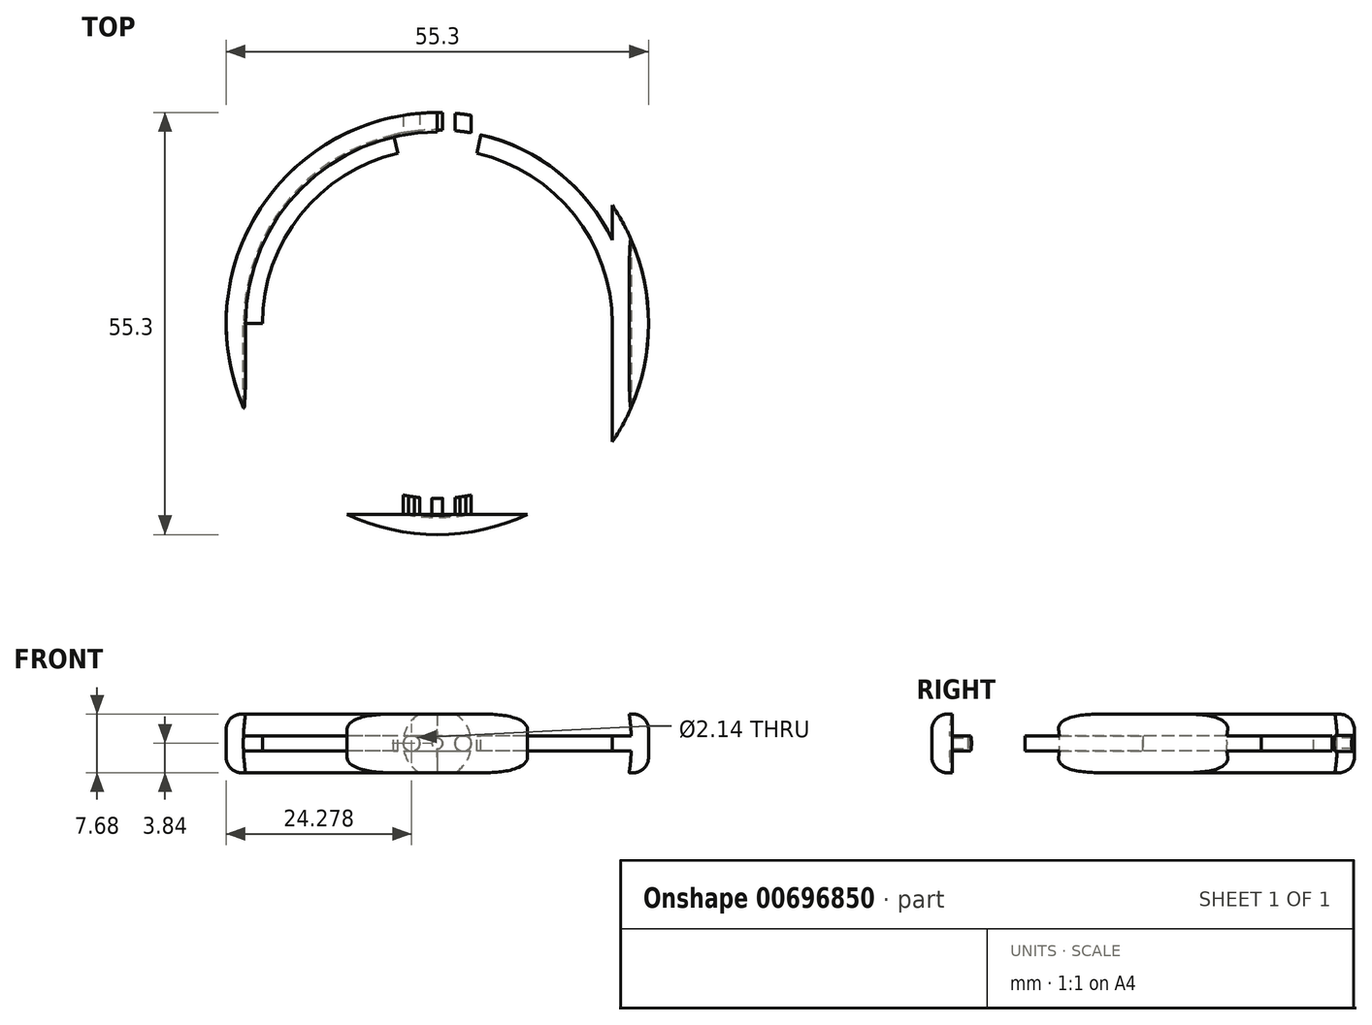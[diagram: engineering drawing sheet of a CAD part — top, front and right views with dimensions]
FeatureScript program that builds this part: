
annotation { "Feature Type Name" : "Feature", "Feature Type Description" : "" }
export const myFeature = defineFeature(function(context is Context, id is Id, definition is map)
    precondition{}
    {
        {
            var Q0;
            Q0=qCreatedBy(makeId("Top.planeOp"),FACE);
            var sketch = newSketch(context, id + "F0", { "sketchPlane" : qUnion([Q0])});
            skCircle(sketch, "E0", {"center": v(0, 0) * mm, "radius": 25.4 * mm});
            skLineSegment(sketch, "E1", {"start": v(-73.41, 0) * mm, "end": v(75.43, 0) * mm});
            skLineSegment(sketch, "E2", {"start": v(0, 25.4) * mm, "end": v(0, -25.4) * mm});
            skCircle(sketch, "E3", {"center": v(0, 0) * mm, "radius": 28.9 * mm});
            skLineSegment(sketch, "E4", {"start": v(-26.6, 11.29) * mm, "end": v(-22.75, 11.29) * mm});
            skLineSegment(sketch, "E5", {"start": v(-26.6, -11.29) * mm, "end": v(-22.75, -11.29) * mm});
            skLineSegment(sketch, "E6", {"start": v(22.75, -11.29) * mm, "end": v(26.6, -11.29) * mm});
            skLineSegment(sketch, "E7", {"start": v(22.75, 11.29) * mm, "end": v(26.6, 11.29) * mm});
            skCircle(sketch, "E8", {"center": v(0, 0) * mm, "radius": 22.72 * mm});
            skCircle(sketch, "E9", {"center": v(0, 0) * mm, "radius": 2.5 * mm});
            skLineSegment(sketch, "E10", {"start": v(0, -25.4) * mm, "end": v(0, -28.9) * mm, "construction": true});
            skSolve(sketch);
        }
        {
            var Q0;
            Q0=qCreatedBy(makeId("Front.planeOp"),FACE);
            var sketch = newSketch(context, id + "F1", { "sketchPlane" : qUnion([Q0])});
            skCircle(sketch, "E11", {"center": v(0, 0) * mm, "radius": 25.4 * mm});
            skLineSegment(sketch, "E12", {"start": v(-25.1, -3.84) * mm, "end": v(-27.65, -3.84) * mm});
            skLineSegment(sketch, "E13", {"start": v(-25.1, 3.84) * mm, "end": v(-27.65, 3.84) * mm});
            skLineSegment(sketch, "E14", {"start": v(-27.65, 3.84) * mm, "end": v(-27.65, -3.84) * mm});
            skLineSegment(sketch, "E15", {"start": v(0, 45.98) * mm, "end": v(0, -45.96) * mm});
            skLineSegment(sketch, "E16", {"start": v(25.38, -1) * mm, "end": v(22.9, -1) * mm});
            skLineSegment(sketch, "E17", {"start": v(22.9, -1) * mm, "end": v(22.9, 1) * mm});
            skLineSegment(sketch, "E18", {"start": v(22.9, 1) * mm, "end": v(25.38, 1) * mm});
            skCircle(sketch, "E19", {"center": v(-3.37, 0) * mm, "radius": 1.07 * mm});
            skCircle(sketch, "E20.MirrorC", {"center": v(3.37, 0) * mm, "radius": 1.07 * mm});
            skCircle(sketch, "E21", {"center": v(0, 0) * mm, "radius": 0.7 * mm});
            skSolve(sketch);
        }
        {
            var Q0;
            {var subQ0=sQuery(id+"F1.wireOp",EDGE,"E12");Q0=makeQuery(id+"F1.imprint","IMPRINT",FACE,{"disambiguationData":[TD([[makeQuery(id+"F1.imprint","IMPRINT",EDGE,{"derivedFrom":subQ0}),-1.0]])]});}
            var Q1;
            Q1=sQuery(id+"F1.wireOp",EDGE,"E15");
            revolve(context, id + "F2", {"entities" : qUnion([Q0]), "axis" : qUnion([Q1]), "revolveType" : RevolveType.FULL});
        }
        {
            var Q0;
            Q0=makeQuery(id+"F2.opRevolve","SWEPT_FACE",FACE,{"disambiguationData":[OSD([sQuery(id+"F1.wireOp",EDGE,"E13")])]});
            var sketch = newSketch(context, id + "F3", { "sketchPlane" : qUnion([Q0])});
            skLineSegment(sketch, "E22", {"start": v(-8.5, -23.63) * mm, "end": v(-8.5, -26.3) * mm});
            skLineSegment(sketch, "E23", {"start": v(8.5, -23.63) * mm, "end": v(8.5, -26.3) * mm});
            skLineSegment(sketch, "E24.MirrorCS", {"start": v(8.5, 23.63) * mm, "end": v(8.5, 26.3) * mm});
            skLineSegment(sketch, "E25.MirrorCS", {"start": v(-8.5, 23.63) * mm, "end": v(-8.5, 26.3) * mm});
            skSolve(sketch);
        }
        {
            var Q0;
            Q0=makeQuery(id+"F2.opRevolve","SWEPT_FACE",FACE,{"disambiguationData":[OSD([sQuery(id+"F1.wireOp",EDGE,"E12")])]});
            var sketch = newSketch(context, id + "F4", { "sketchPlane" : qUnion([Q0])});
            skLineSegment(sketch, "E26", {"start": v(-8.5, -26.3) * mm, "end": v(-8.5, -23.63) * mm});
            skLineSegment(sketch, "E27", {"start": v(8.5, -26.3) * mm, "end": v(8.5, -23.63) * mm});
            skLineSegment(sketch, "E28.MirrorCS", {"start": v(-8.5, 26.3) * mm, "end": v(-8.5, 23.63) * mm});
            skLineSegment(sketch, "E29.MirrorCS", {"start": v(8.5, 26.3) * mm, "end": v(8.5, 23.63) * mm});
            skSolve(sketch);
        }
        {
            var Q0;
            {var subQ0=sQuery(id+"F1.wireOp",EDGE,"E14");var subQ1=sQuery(id+"F1.wireOp",EDGE,"E13");Q0=makeQuery(id+"FaxaOUovcLgCMh0_1.boolean.opBoolean","SPLIT",EDGE,{"disambiguationData":[TD([makeQuery(id+"FSwHRoq1Rwb6Aft_1.opRevolve","SWEPT_FACE",FACE,{"disambiguationData":[OSD([sQuery(id+"F3.wireOp",EDGE,"E24.MirrorCS")])]})])],"derivedFrom":makeQuery(id+"FSwHRoq1Rwb6Aft_1.boolean.opBoolean","SPLIT",EDGE,{"derivedFrom":makeQuery(id+"F2.opRevolve","SWEPT_EDGE",EDGE,{"disambiguationData":[OSD([subQ1,subQ0])]})})});}
            var Q1;
            {var subQ0=sQuery(id+"F1.wireOp",EDGE,"E14");var subQ1=sQuery(id+"F1.wireOp",EDGE,"E12");Q1=makeQuery(id+"FmTKT4PjjMc3EsV_1.boolean.opBoolean","SPLIT",EDGE,{"disambiguationData":[TD([makeQuery(id+"FSOl6FTe3INRHHG_1.opRevolve","SWEPT_FACE",FACE,{"disambiguationData":[OSD([sQuery(id+"F4.wireOp",EDGE,"E27")])]})])],"derivedFrom":makeQuery(id+"FSOl6FTe3INRHHG_1.boolean.opBoolean","SPLIT",EDGE,{"derivedFrom":makeQuery(id+"F2.opRevolve","SWEPT_EDGE",EDGE,{"disambiguationData":[OSD([subQ1,subQ0])]})})});}
            var Q2;
            {var subQ0=sQuery(id+"F1.wireOp",EDGE,"E14");var subQ1=sQuery(id+"F1.wireOp",EDGE,"E13");Q2=makeQuery(id+"FaxaOUovcLgCMh0_1.boolean.opBoolean","SPLIT",EDGE,{"disambiguationData":[TD([makeQuery(id+"FSwHRoq1Rwb6Aft_1.opRevolve","SWEPT_FACE",FACE,{"disambiguationData":[OSD([sQuery(id+"F3.wireOp",EDGE,"E25.MirrorCS")])]})])],"derivedFrom":makeQuery(id+"FSwHRoq1Rwb6Aft_1.boolean.opBoolean","SPLIT",EDGE,{"derivedFrom":makeQuery(id+"F2.opRevolve","SWEPT_EDGE",EDGE,{"disambiguationData":[OSD([subQ1,subQ0])]})})});}
            var Q3;
            {var subQ0=sQuery(id+"F1.wireOp",EDGE,"E14");var subQ1=sQuery(id+"F1.wireOp",EDGE,"E12");Q3=makeQuery(id+"FmTKT4PjjMc3EsV_1.boolean.opBoolean","SPLIT",EDGE,{"disambiguationData":[TD([makeQuery(id+"FSOl6FTe3INRHHG_1.opRevolve","SWEPT_FACE",FACE,{"disambiguationData":[OSD([sQuery(id+"F4.wireOp",EDGE,"E26")])]})])],"derivedFrom":makeQuery(id+"FSOl6FTe3INRHHG_1.boolean.opBoolean","SPLIT",EDGE,{"derivedFrom":makeQuery(id+"F2.opRevolve","SWEPT_EDGE",EDGE,{"disambiguationData":[OSD([subQ1,subQ0])]})})});}
            fillet(context, id + "F5", {"entities" : qUnion([Q0, Q1, Q2, Q3]), "radius" : 2 * mm, "tangentPropagation" : true, "allowEdgeOverflow" : false});
        }
        {
            var Q0;
            Q0=makeQuery(id+"F1.imprint","IMPRINT",FACE,{"disambiguationData":[TD([[makeQuery(id+"F1.imprint","IMPRINT",EDGE,{"derivedFrom":sQuery(id+"F1.wireOp",EDGE,"E20.MirrorC")}),-1.0]])]});
            var Q1;
            Q1=makeQuery(id+"F1.imprint","IMPRINT",FACE,{"disambiguationData":[TD([[makeQuery(id+"F1.imprint","IMPRINT",EDGE,{"derivedFrom":sQuery(id+"F1.wireOp",EDGE,"E19")}),1.0]])]});
            extrude(context, id + "F6", {"entities" : qUnion([Q0, Q1]), "operationType" : NewBodyOperationType.REMOVE, "oppositeDirection" : true, "depth" : 43.9 * mm, "offsetDistance" : 25 * mm});
        }
        {
            var Q0;
            {var subQ0=sQuery(id+"F1.wireOp",EDGE,"E16");Q0=makeQuery(id+"F1.imprint","IMPRINT",FACE,{"disambiguationData":[TD([[makeQuery(id+"F1.imprint","IMPRINT",EDGE,{"derivedFrom":subQ0}),-1.0]])]});}
            var Q1;
            Q1=sQuery(id+"F1.wireOp",EDGE,"E15");
            revolve(context, id + "F7", {"operationType" : NewBodyOperationType.ADD, "entities" : qUnion([Q0]), "axis" : qUnion([Q1]), "revolveType" : RevolveType.TWO_DIRECTIONS, "angle" : 257 * degree, "angleBack" : 100 * degree});
        }
        {
            var Q0;
            {var subQ0=sQuery(id+"F1.wireOp",EDGE,"E16");Q0=makeQuery(id+"F1.imprint","IMPRINT",FACE,{"disambiguationData":[TD([[makeQuery(id+"F1.imprint","IMPRINT",EDGE,{"derivedFrom":subQ0}),-1.0]])]});}
            var Q1;
            Q1=sQuery(id+"F1.wireOp",EDGE,"E15");
            revolve(context, id + "F8", {"operationType" : NewBodyOperationType.ADD, "entities" : qUnion([Q0]), "axis" : qUnion([Q1]), "revolveType" : RevolveType.TWO_DIRECTIONS, "angle" : 100 * degree, "angleBack" : 283 * degree});
        }
        {
            var Q0;
            {var subQ0=sQuery(id+"F1.wireOp",EDGE,"E21");var subQ1=sQuery(id+"F1.wireOp",EDGE,"E15");var subQ2=makeQuery(id+"F1.imprint","INTERSECT",VERTEX,{"disambiguationData":[OD(0.0)],"derivedFrom":[subQ1,subQ0]});Q0=makeQuery(id+"F1.imprint","IMPRINT",FACE,{"disambiguationData":[TD([[makeQuery(id+"F1.imprint","IMPRINT",EDGE,{"disambiguationData":[TD([[subQ2,-1.0]])],"derivedFrom":subQ1}),-1.0]])]});}
            var Q1;
            {var subQ0=sQuery(id+"F1.wireOp",EDGE,"E21");var subQ1=sQuery(id+"F1.wireOp",EDGE,"E15");var subQ2=makeQuery(id+"F1.imprint","INTERSECT",VERTEX,{"disambiguationData":[OD(0.0)],"derivedFrom":[subQ1,subQ0]});Q1=makeQuery(id+"F1.imprint","IMPRINT",FACE,{"disambiguationData":[TD([[makeQuery(id+"F1.imprint","IMPRINT",EDGE,{"disambiguationData":[TD([[subQ2,-1.0]])],"derivedFrom":subQ1}),1.0]])]});}
            extrude(context, id + "F9", {"entities" : qUnion([Q0, Q1]), "operationType" : NewBodyOperationType.REMOVE, "depth" : 25 * mm, "offsetDistance" : 25 * mm});
        }
    });
